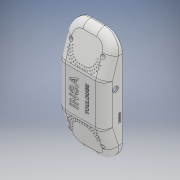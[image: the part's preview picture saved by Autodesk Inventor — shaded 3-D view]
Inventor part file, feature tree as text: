
AUTODESK INVENTOR PART (.ipt)
format: ipt  version: 2019 (Build 230136000, 136)  size: 964,096 bytes
history: native  units: mm
features: sketch x15, extrude x14, chamfer x2, fillet x2, shell x1, other x1
ambient origin geometry x8: Origin, YZ Plane, XZ Plane, XY Plane, X Axis, Y Axis, Z Axis, Center Point
bodies: Solide1 (feature_tree)
feature tree (35):
  extrude  "Extrusion1"  Depth=200.0mm
  extrude  "Extrusion11"  Depth=85.0mm
  chamfer  "Chanfrein1"  Distance=42.5mm
  chamfer  "Chanfrein2"  Distance=100.0mm
  fillet  "Congé3"  Radius=34.0mm
  fillet  "Congé4"  Radius=20.0mm
  shell  "Coque1"  Thickness=20.0mm
  extrude  "Extrusion2"  Depth=30.0mm
  extrude  "Extrusion3"  Depth=15.0mm
  extrude  "Extrusion4"  Depth=2.5mm
  extrude  "Extrusion5"  Depth=2.5mm TaperAngle=0.0deg
  extrude  "Extrusion6"  Depth=108.0mm
  extrude  "Extrusion7"  Depth=70.0mm
  extrude  "Extrusion8"  Depth=35.0mm
  extrude  "Extrusion9"  Depth=54.0mm
  extrude  "Extrusion12"  Depth=10.0mm
  extrude  "Extrusion13"  Depth=10.0mm
  extrude  "Extrusion14"  Depth=10.0mm
  other  "Gravure1"
  extrude  "Extrusion15"  Depth=10.0mm
  sketch  "Esquisse1"
  sketch  "Esquisse3"
  sketch  "Esquisse4"
  sketch  "Esquisse5"
  sketch  "Esquisse6"
  sketch  "Esquisse7"
  sketch  "Esquisse8"
  sketch  "Esquisse9"
  sketch  "Esquisse10"
  sketch  "Esquisse11"
  sketch  "Esquisse14"
  sketch  "Esquisse15"
  sketch  "Esquisse16"
  sketch  "Esquisse17"
  sketch  "Esquisse18"
